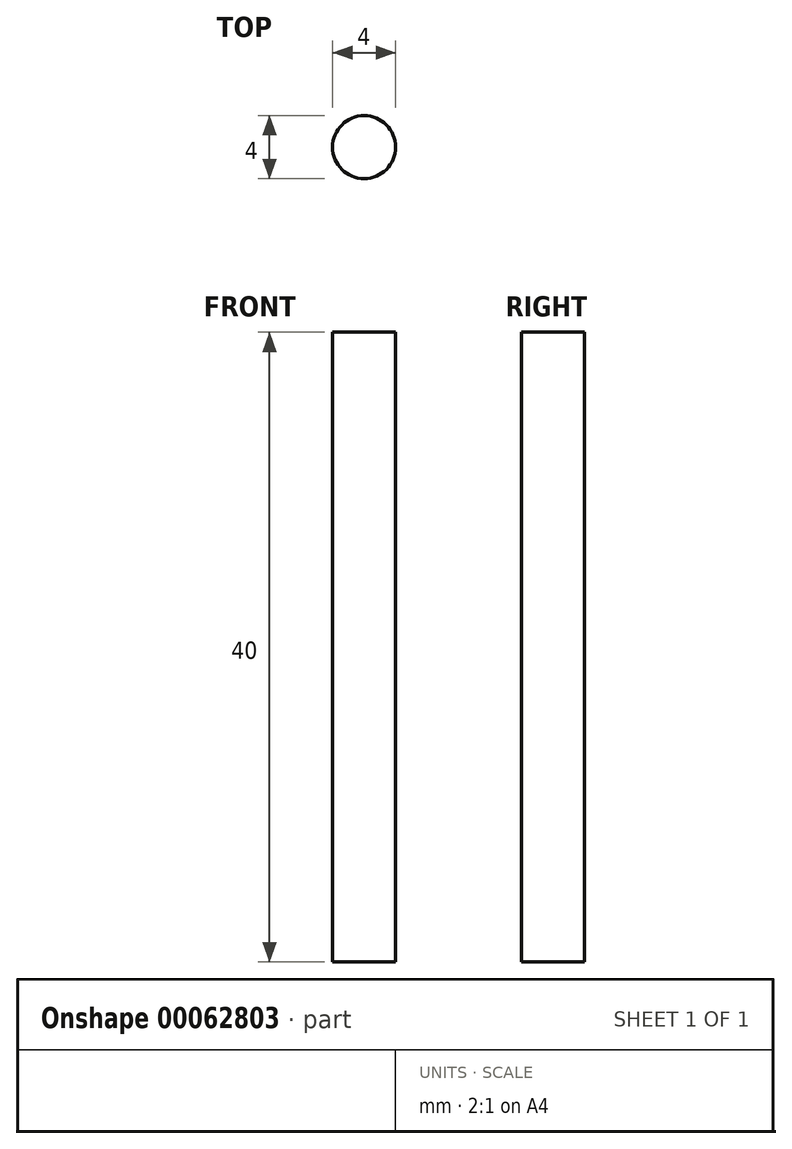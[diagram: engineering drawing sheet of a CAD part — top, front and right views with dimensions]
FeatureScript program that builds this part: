
annotation { "Feature Type Name" : "Feature", "Feature Type Description" : "" }
export const myFeature = defineFeature(function(context is Context, id is Id, definition is map)
    precondition{}
    {
        {
            var Q0;
            Q0=qCreatedBy(makeId("Top.planeOp"),FACE);
            var sketch = newSketch(context, id + "F0", { "sketchPlane" : qUnion([Q0])});
            skCircle(sketch, "E0", {"center": v(0, 0) * mm, "radius": 2 * mm});
            skSolve(sketch);
        }
        {
            var Q0;
            Q0=makeQuery(id+"F0.imprint","IMPRINT",FACE,{"disambiguationData":[TD([[makeQuery(id+"F0.imprint","IMPRINT",EDGE,{"derivedFrom":sQuery(id+"F0.wireOp",EDGE,"E0")}),1.0]])]});
            extrude(context, id + "F1", {"entities" : qUnion([Q0]), "depth" : 40 * mm});
        }
    });
